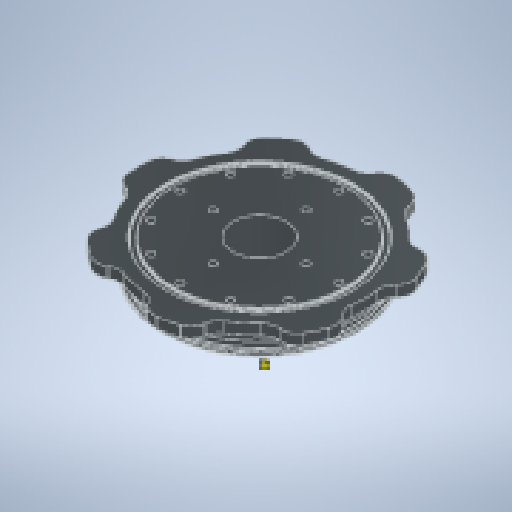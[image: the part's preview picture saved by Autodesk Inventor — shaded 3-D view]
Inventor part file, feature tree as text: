
AUTODESK INVENTOR PART (.ipt)
format: ipt  version: 2024.3 (Build 283343000, 343)  size: 479,744 bytes
history: native  units: mm
features: sketch x3, hole x3, fillet x2, other x1, revolve x1, extrude x1, pattern_circular x1, chamfer x1
ambient origin geometry x8: Origin, YZ Plane, XZ Plane, XY Plane, X Axis, Y Axis, Z Axis, Center Point
bodies: Body1 (feature_tree)
feature tree (13):
  other  "Sólido1"
  revolve  "Revolución1"  [1 undecoded]
  fillet  "Empalme1"  Radius=0.872665mm
  sketch  "Boceto2"  dims[d7=94.0mm d9=0.275mm d10=2.1mm]
  extrude  "Extrusión1"  Depth=0.275mm
  fillet  "Empalme3"  Radius=2.1mm
  pattern_circular  "Patrón circular2"  Angle=90.0deg  [1 undecoded]
  hole  "Agujero3"  [1 undecoded]
  sketch  "Boceto5"  dims[d11=3.7mm d12=90.0deg d13=0.25mm d14=89.8mm d17=4.363323mm d18=57.5mm d19=10.0mm d20=0.0mm d32=82.27mm d33=2.5mm d34=0.872665mm d35=0.275mm d36=1.3mm d44=20.0mm d45=7.5mm d46=7.5mm d47=70.0mm d48=360.0deg d51=31.0mm d52=3.4mm d53=8.5mm d54=4.0mm d55=2.0mm d56=90.0deg d57=10.0mm d58=120.0deg d59=37.5mm d60=120.0mm d62=360.0deg d64=3.4mm d65=6.0mm d66=3.023mm d67=2.0mm d68=14.3117mm d69=8.0mm d70=20.594885mm d71=90.0deg d72=3.4mm d73=6.0mm d74=6.3mm d75=2.0mm d76=90.0deg d77=8.0mm d78=20.594885mm d79=0.0mm d80=0.0mm d81=0.0mm d82=2.0mm d83=2.0mm d84=45.0deg]
  hole  "Agujero4"  [1 undecoded]
  hole  "Agujero5"  [1 undecoded]
  chamfer  "Chaflán1"  Distance=57.5mm
  sketch  "Boceto1"  dims[d1=5.0mm d4=25.0mm d6=0.872665mm]
note: 5 required parameter values undecoded (feature->parameter linkage not recoverable at this tier; creation-order binding heuristic only, values carry confidence <= 0.55)